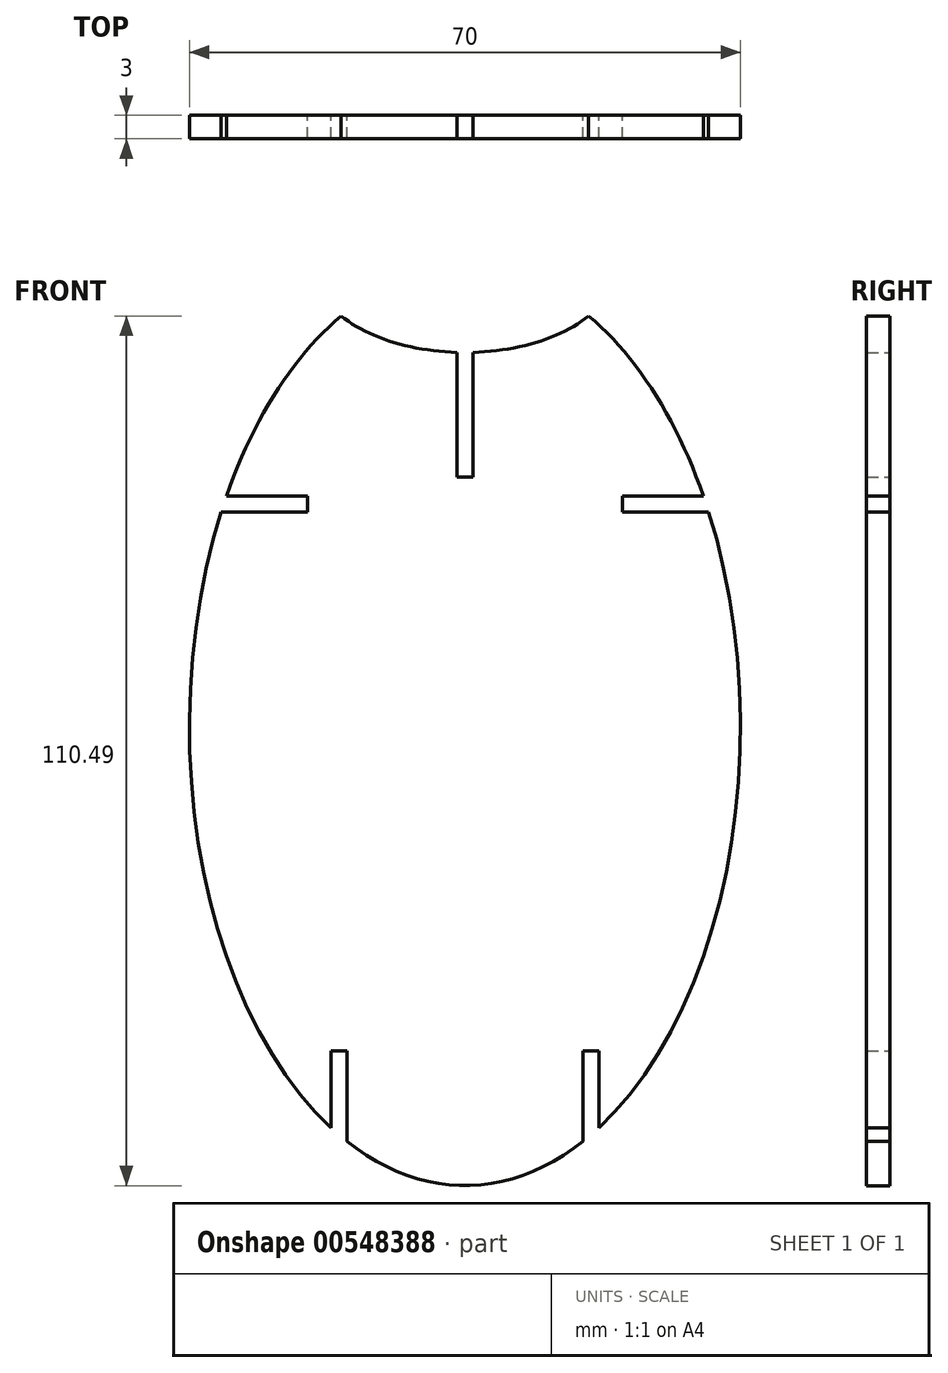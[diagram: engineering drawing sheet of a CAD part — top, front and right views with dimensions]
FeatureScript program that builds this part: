
annotation { "Feature Type Name" : "Feature", "Feature Type Description" : "" }
export const myFeature = defineFeature(function(context is Context, id is Id, definition is map)
    precondition{}
    {
        {
            var Q0;
            Q0=qCreatedBy(makeId("Front.planeOp"),FACE);
            var sketch = newSketch(context, id + "F0", { "sketchPlane" : qUnion([Q0])});
            skEllipse(sketch, "E0", {"center": v(0, 0) * mm, "majorRadius": 58.35 * mm, "minorRadius": 35 * mm, "majorAxis": v(0, -1)});
            skSolve(sketch);
        }
        {
            var Q0;
            Q0=qSketchRegion(id+"F0",true);
            extrude(context, id + "F1", {"entities" : qUnion([Q0]), "depth" : 3 * mm});
        }
        {
            var Q0;
            Q0=qCreatedBy(makeId("Front.planeOp"),FACE);
            var sketch = newSketch(context, id + "F2", { "sketchPlane" : qUnion([Q0])});
            skLineSegment(sketch, "E1.bottom", {"start": v(-49.47, 29.24) * mm, "end": v(-20, 29.24) * mm});
            skLineSegment(sketch, "E1.top", {"start": v(-49.47, 27.24) * mm, "end": v(-20, 27.24) * mm});
            skLineSegment(sketch, "E1.left", {"start": v(-49.47, 29.24) * mm, "end": v(-49.47, 27.24) * mm});
            skLineSegment(sketch, "E1.right", {"start": v(-20, 29.24) * mm, "end": v(-20, 27.24) * mm});
            skLineSegment(sketch, "E2.MirrorCS", {"start": v(49.47, 29.24) * mm, "end": v(20, 29.24) * mm});
            skLineSegment(sketch, "E3.MirrorCS", {"start": v(49.47, 27.24) * mm, "end": v(20, 27.24) * mm});
            skLineSegment(sketch, "E4.MirrorCS", {"start": v(20, 29.24) * mm, "end": v(20, 27.24) * mm});
            skLineSegment(sketch, "E5.MirrorCS", {"start": v(49.47, 29.24) * mm, "end": v(49.47, 27.24) * mm});
            skSolve(sketch);
        }
        {
            var Q0;
            Q0=qSketchRegion(id+"F2",true);
            extrude(context, id + "F3", {"entities" : qUnion([Q0]), "operationType" : NewBodyOperationType.REMOVE, "depth" : 25 * mm});
        }
        {
            var Q0;
            Q0=qCreatedBy(makeId("Front.planeOp"),FACE);
            var sketch = newSketch(context, id + "F4", { "sketchPlane" : qUnion([Q0])});
            skLineSegment(sketch, "E6.bottom", {"start": v(-17, -41.2) * mm, "end": v(-15, -41.2) * mm});
            skLineSegment(sketch, "E6.left", {"start": v(-17, -41.2) * mm, "end": v(-17, -51.2) * mm});
            skLineSegment(sketch, "E6.right", {"start": v(-15, -41.2) * mm, "end": v(-15, -53.12) * mm});
            skLineSegment(sketch, "E7.MirrorCS", {"start": v(17, -41.2) * mm, "end": v(17, -51.2) * mm});
            skLineSegment(sketch, "E8.MirrorCS", {"start": v(15, -41.2) * mm, "end": v(15, -53.12) * mm});
            skLineSegment(sketch, "E9.MirrorCS", {"start": v(17, -41.2) * mm, "end": v(15, -41.2) * mm});
            skLineSegment(sketch, "E10", {"start": v(-17, -51.2) * mm, "end": v(-17, -64.54) * mm});
            skLineSegment(sketch, "E11", {"start": v(-15, -53.12) * mm, "end": v(-15, -64.63) * mm});
            skLineSegment(sketch, "E12", {"start": v(15, -53.12) * mm, "end": v(15, -64.63) * mm});
            skLineSegment(sketch, "E13", {"start": v(17, -51.2) * mm, "end": v(17, -64.63) * mm});
            skLineSegment(sketch, "E14", {"start": v(-17, -64.54) * mm, "end": v(-15, -64.63) * mm});
            skLineSegment(sketch, "E15", {"start": v(15, -64.63) * mm, "end": v(17, -64.63) * mm});
            skSolve(sketch);
        }
        {
            var Q0;
            Q0=qSketchRegion(id+"F4",true);
            extrude(context, id + "F5", {"entities" : qUnion([Q0]), "operationType" : NewBodyOperationType.REMOVE, "depth" : 10 * mm});
        }
        {
            var Q0;
            Q0=qCreatedBy(makeId("Front.planeOp"),FACE);
            var sketch = newSketch(context, id + "F6", { "sketchPlane" : qUnion([Q0])});
            skEllipse(sketch, "E16", {"center": v(0, 58.2) * mm, "majorRadius": 19.07 * mm, "minorRadius": 10.7 * mm, "majorAxis": v(1, 0)});
            skSolve(sketch);
        }
        {
            var Q0;
            Q0=qSketchRegion(id+"F6",true);
            extrude(context, id + "F7", {"entities" : qUnion([Q0]), "operationType" : NewBodyOperationType.REMOVE, "depth" : 25 * mm});
        }
        {
            var Q0;
            Q0=qCreatedBy(makeId("Front.planeOp"),FACE);
            var sketch = newSketch(context, id + "F8", { "sketchPlane" : qUnion([Q0])});
            skLineSegment(sketch, "E17.bottom", {"start": v(-1, 56.7) * mm, "end": v(0, 56.7) * mm});
            skLineSegment(sketch, "E17.top", {"start": v(-1, 31.7) * mm, "end": v(0, 31.7) * mm});
            skLineSegment(sketch, "E17.left", {"start": v(-1, 56.7) * mm, "end": v(-1, 31.7) * mm});
            skLineSegment(sketch, "E17.right", {"start": v(0, 56.7) * mm, "end": v(0, 31.7) * mm});
            skLineSegment(sketch, "E18.MirrorCS", {"start": v(1, 31.7) * mm, "end": v(0, 31.7) * mm});
            skLineSegment(sketch, "E19.MirrorCS", {"start": v(1, 56.7) * mm, "end": v(1, 31.7) * mm});
            skLineSegment(sketch, "E20.MirrorCS", {"start": v(1, 56.7) * mm, "end": v(0, 56.7) * mm});
            skSolve(sketch);
        }
        {
            var Q0;
            Q0=qSketchRegion(id+"F8",true);
            extrude(context, id + "F9", {"entities" : qUnion([Q0]), "operationType" : NewBodyOperationType.REMOVE, "depth" : 25 * mm});
        }
    });
